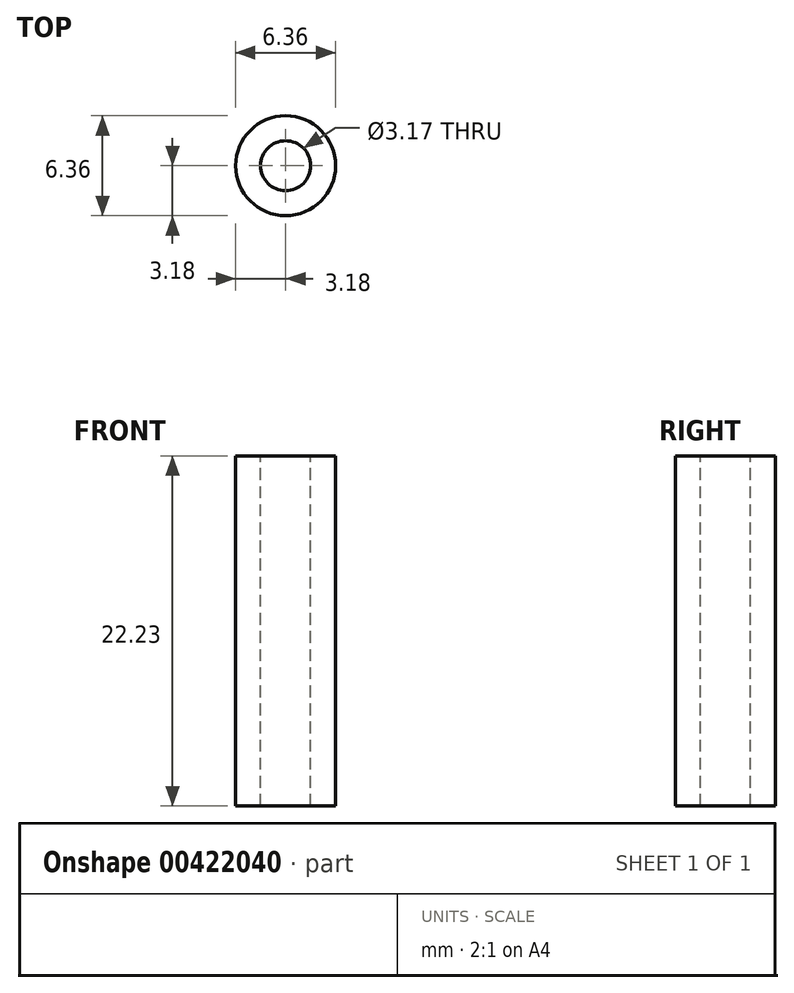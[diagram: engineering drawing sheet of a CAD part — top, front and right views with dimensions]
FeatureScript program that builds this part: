
annotation { "Feature Type Name" : "Feature", "Feature Type Description" : "" }
export const myFeature = defineFeature(function(context is Context, id is Id, definition is map)
    precondition{}
    {
        {
            var Q0;
            Q0=qCreatedBy(makeId("Front.planeOp"),FACE);
            var sketch = newSketch(context, id + "F0", { "sketchPlane" : qUnion([Q0])});
            skLineSegment(sketch, "E0", {"start": v(-3.18, 0) * mm, "end": v(-3.18, 22.23) * mm});
            skLineSegment(sketch, "E1", {"start": v(0, 0) * mm, "end": v(0, 22.23) * mm});
            skLineSegment(sketch, "E2", {"start": v(-3.18, 22.23) * mm, "end": v(0, 22.23) * mm});
            skLineSegment(sketch, "E3", {"start": v(-3.18, 0) * mm, "end": v(0, 0) * mm});
            skSolve(sketch);
        }
        {
            var Q0;
            Q0 = qSketchRegion(id + "F0", true);
            var Q1;
            Q1=sQuery(id+"F0.wireOp",EDGE,"E1");
            revolve(context, id + "F1", {"entities" : qUnion([Q0]), "axis" : qUnion([Q1]), "revolveType" : RevolveType.FULL});
        }
        {
            var Q0;
            Q0=makeQuery(id+"F1.opRevolve","SWEPT_FACE",FACE,{"disambiguationData":[OSD([sQuery(id+"F0.wireOp",EDGE,"E2")])]});
            var sketch = newSketch(context, id + "F2", { "sketchPlane" : qUnion([Q0])});
            skCircle(sketch, "E4", {"center": v(0, 0) * mm, "radius": 1.59 * mm});
            skSolve(sketch);
        }
        {
            var Q0;
            Q0=makeQuery(id+"F2.imprint","IMPRINT",FACE,{"disambiguationData":[TD([[makeQuery(id+"F2.imprint","IMPRINT",EDGE,{"derivedFrom":sQuery(id+"F2.wireOp",EDGE,"E4")}),1.0]])]});
            extrude(context, id + "F3", {"entities" : qUnion([Q0]), "operationType" : NewBodyOperationType.REMOVE, "endBound" : BoundingType.UP_TO_NEXT, "oppositeDirection" : true, "depth" : 25.4 * mm});
        }
    });
